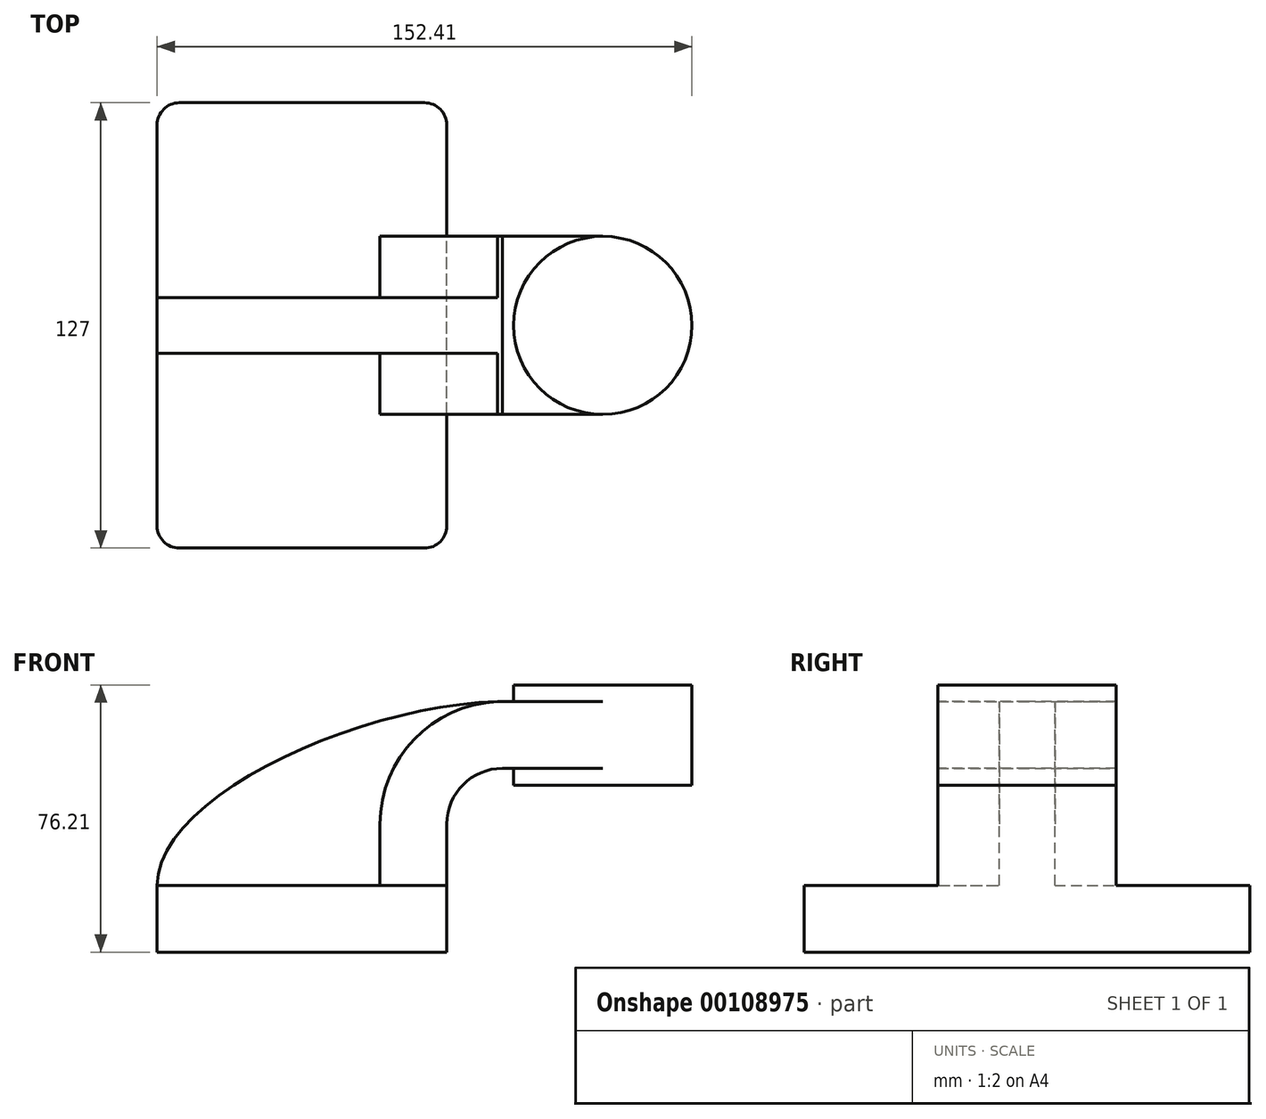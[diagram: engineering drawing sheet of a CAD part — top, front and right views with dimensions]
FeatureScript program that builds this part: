
annotation { "Feature Type Name" : "Feature", "Feature Type Description" : "" }
export const myFeature = defineFeature(function(context is Context, id is Id, definition is map)
    precondition{}
    {
        {
            var Q0;
            Q0=qCreatedBy(makeId("Front.planeOp"),FACE);
            var sketch = newSketch(context, id + "F0", { "sketchPlane" : qUnion([Q0])});
            skLineSegment(sketch, "E0.bottom", {"start": v(-41.28, 9.52) * mm, "end": v(41.28, 9.53) * mm});
            skLineSegment(sketch, "E0.top", {"start": v(-41.28, -9.53) * mm, "end": v(41.28, -9.53) * mm});
            skLineSegment(sketch, "E0.left", {"start": v(-41.28, 9.52) * mm, "end": v(-41.27, -9.53) * mm});
            skLineSegment(sketch, "E0.right", {"start": v(41.28, 9.53) * mm, "end": v(41.28, -9.52) * mm});
            skPoint(sketch, "E0.middle", {"position": v(0, 0) * mm});
            skLineSegment(sketch, "E1", {"start": v(41.27, 9.53) * mm, "end": v(41.27, 27) * mm});
            skLineSegment(sketch, "E2.bottom", {"start": v(60.32, 66.68) * mm, "end": v(111.12, 66.68) * mm});
            skLineSegment(sketch, "E2.top", {"start": v(60.32, 38.1) * mm, "end": v(111.12, 38.1) * mm});
            skLineSegment(sketch, "E2.left", {"start": v(60.32, 66.68) * mm, "end": v(60.32, 38.1) * mm});
            skLineSegment(sketch, "E2.right", {"start": v(111.12, 66.68) * mm, "end": v(111.12, 38.1) * mm});
            skPoint(sketch, "E2.middle", {"position": v(85.72, 52.39) * mm});
            skArc(sketch, "E3", {"start": v(41.27, 27) * mm, "mid": v(45.92, 38.23) * mm, "end": v(57.15, 42.88) * mm});
            skLineSegment(sketch, "E4", {"start": v(57.15, 42.88) * mm, "end": v(85.72, 42.88) * mm});
            skLineSegment(sketch, "E5.0", {"start": v(57.15, 61.93) * mm, "end": v(85.72, 61.93) * mm});
            skArc(sketch, "E5.1", {"start": v(22.22, 27) * mm, "mid": v(32.45, 51.7) * mm, "end": v(57.15, 61.93) * mm});
            skLineSegment(sketch, "E5.2", {"start": v(22.22, 9.53) * mm, "end": v(22.22, 27) * mm});
            skLineSegment(sketch, "E6", {"start": v(85.72, 38.1) * mm, "end": v(85.72, 66.68) * mm});
            skFitSpline(sketch, "E7", {"points": [v(-41.28, 9.52) * mm, v(57.15, 61.93) * mm], "startDerivative": vector(0.35, 76.86) * mm, "endDerivative": vector(120.01, 1.56) * mm});
            skSolve(sketch);
        }
        {
            var Q0;
            Q0=makeQuery(id+"F0.imprint","IMPRINT",FACE,{"disambiguationData":[TD([[makeQuery(id+"F0.imprint","IMPRINT",EDGE,{"derivedFrom":sQuery(id+"F0.wireOp",EDGE,"E0.top")}),1.0]])]});
            extrude(context, id + "F1", {"entities" : qUnion([Q0]), "endBound" : BoundingType.SYMMETRIC, "depth" : 127 * mm});
        }
        {
            var Q0;
            {var subQ6=sQuery(id+"F0.wireOp",EDGE,"E1");Q0=makeQuery(id+"F0.imprint","IMPRINT",FACE,{"disambiguationData":[TD([[makeQuery(id+"F0.imprint","IMPRINT",EDGE,{"derivedFrom":subQ6}),1.0]])]});}
            var Q1;
            {var subQ0=sQuery(id+"F0.wireOp",EDGE,"E5.0");var subQ1=sQuery(id+"F0.wireOp",EDGE,"E2.left");var subQ2=makeQuery(id+"F0.imprint","INTERSECT",VERTEX,{"derivedFrom":[subQ1,subQ0]});Q1=makeQuery(id+"F0.imprint","IMPRINT",FACE,{"disambiguationData":[TD([[makeQuery(id+"F0.imprint","IMPRINT",EDGE,{"disambiguationData":[TD([[subQ2,-1.0]])],"derivedFrom":subQ1}),1.0]])]});}
            extrude(context, id + "F2", {"entities" : qUnion([Q0, Q1]), "operationType" : NewBodyOperationType.ADD, "endBound" : BoundingType.SYMMETRIC, "depth" : 50.8 * mm});
        }
        {
            var Q0;
            {var subQ3=sQuery(id+"F0.wireOp",EDGE,"E5.2");Q0=makeQuery(id+"F0.imprint","IMPRINT",FACE,{"disambiguationData":[TD([[makeQuery(id+"F0.imprint","IMPRINT",EDGE,{"derivedFrom":subQ3}),1.0]])]});}
            extrude(context, id + "F3", {"entities" : qUnion([Q0]), "operationType" : NewBodyOperationType.ADD, "endBound" : BoundingType.SYMMETRIC, "depth" : 15.88 * mm});
        }
        {
            var Q0;
            {var subQ0=sQuery(id+"F0.wireOp",EDGE,"E2.right");Q0=makeQuery(id+"F0.imprint","IMPRINT",FACE,{"disambiguationData":[TD([[makeQuery(id+"F0.imprint","IMPRINT",EDGE,{"derivedFrom":subQ0}),-1.0]])]});}
            var Q1;
            Q1=sQuery(id+"F0.wireOp",EDGE,"E6");
            revolve(context, id + "F4", {"operationType" : NewBodyOperationType.ADD, "entities" : qUnion([Q0]), "axis" : qUnion([Q1]), "revolveType" : RevolveType.FULL});
        }
        {
            var Q0;
            Q0=makeQuery(id+"F1.opExtrude","CAP_EDGE",EDGE,{"disambiguationData":[OSD([sQuery(id+"F0.wireOp",EDGE,"E0.left")])],"isStart":false});
            var Q1;
            Q1=makeQuery(id+"F1.opExtrude","CAP_EDGE",EDGE,{"disambiguationData":[OSD([sQuery(id+"F0.wireOp",EDGE,"E0.right")])],"isStart":false});
            var Q2;
            Q2=makeQuery(id+"F1.opExtrude","CAP_EDGE",EDGE,{"disambiguationData":[OSD([sQuery(id+"F0.wireOp",EDGE,"E0.left")])],"isStart":true});
            var Q3;
            Q3=makeQuery(id+"F1.opExtrude","CAP_EDGE",EDGE,{"disambiguationData":[OSD([sQuery(id+"F0.wireOp",EDGE,"E0.right")])],"isStart":true});
            fillet(context, id + "F5", {"entities" : qUnion([Q0, Q1, Q2, Q3]), "radius" : 6.35 * mm, "tangentPropagation" : true, "allowEdgeOverflow" : false});
        }
    });
